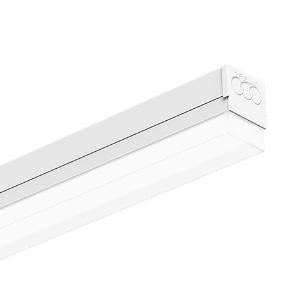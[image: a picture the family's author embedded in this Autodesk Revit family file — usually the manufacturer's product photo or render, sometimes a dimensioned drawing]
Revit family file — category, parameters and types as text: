
# Revit family: 3f_filippi_-_3f_zeta_dr_3f_filippi_-_10986_-_3f_zeta_dr_2x22_led_ep_l1489
name_source: partatom
category: Lighting Fixtures
units: mm (PartAtom-declared; Revit-internal decimal feet)

## family parameters
Cut with Voids When Loaded = No
Host = Face
Light Source = No
Part Type = Normal
Room Calculation Point = No
Round Connector Dimension = Use Diameter
Shared = No

## types (1)
- 3F Filippi - 3F Zeta DR (1 x LED, 6253 lm, 50 W, 4000 K)
    Apparent Load = 50 VA
    Approval mark = ENEC
    CIE Flux Codes = 41 72 91 86 100
    Color Rendering = 80
    Color Temperature = 4000 K
    Control Gear = Electronic ballast
    Default Elevation = 1800 mm
    Description = ILLUMINOTECHNICAL
Luminous efficiency 100% (DLOR 86%, ULOR 14%).
Initial luminous flux of the luminaire 6253 lm.
Emergency luminaire luminous flux BLF 7.6%.
Diffused symmetric distribution.
Installation Interdistance Transv.D = 1.31 x hu - Long.D = 1.25 x hu.
Tabular UGR (CIE 117 - 4H-8H; S=0.25H; 70/50/20): RUG 25.7 - 24.2.
Beam angle: 136° - 112°.
Luminous efficacy 125 lm/W.
Lifetime (L93/B10): 30000 h. (tq+25°C)
Lifetime (L90/B10): 50000 h. (tq+25°C)
Lifetime (L85/B10): 80000 h. (tq+25°C)
Lifetime (L80/B10): 100000 h. (tq+25°C)
Sudden decreased luminous flux after 50000 hours: 0% (C0).
Photobiological safety in compliance with IEC/TR 62778: RG0 risk exempt, (IEC 62471).
In compliance with IEC/EN 62722-2-1 - IEC/EN 62717 standards.

SOURCE
2 linear LED modules 22W/840.
Energy efficiency class (UE 2019/2020 - UE 2019/2015): D.
CIE 13.3 Colour rendering index: CRI >80 (R9 <50%).
IES TM-30 Fidelity Index: Rf = 84 Rg = 95.
CCT nominal colour temperature 4000 K.
Colour initial tolerance (MacAdam): SDCM 3.

MECHANICAL
Housing in hot-galvanised steel, painted in white polyester, obtained through rolling process.
Light unit in hot-galvanised steel, painted in white polyester base with fixing springs and retractable safety hooks in stainless steel.
Rectangular screen in self-extinguishing polycarbonate, UV stabilised, opal, with smooth outer surface.
End caps in white polycarbonate.
Pair of stainless steel sliding brackets with sliding block screws.
Luminaire with limited surface temperature. - D - (EN 60598-2-24)
Dimensions: 1489x62 mm, height 81 mm. Weight 4.76 kg.
IP40 protection degree.
Mechanical strength to impacts IK06 (1 joule).
Glow-wire test resistance 850°C.

ELECTRICAL
Halogen Free electronic wiring 230V-50/60Hz, power factor 0.90, THD <25%, constant output current, SELV, class I, 1 driver.
Power of the luminaire 50 W.
CE - IEC 60598-1 - EN 60598-1.
EP maintained emergency wiring on board, 1h duration, 24h recharge; compliant with EN 60598-2-22, excluding high risk areas.
SAFE FLICKER: PstLM=<1 and SVM=<0.4 (IEC TR 61547-1 and IEC TR 63158), to ensure a more comfortable and safe light.
Ambient temperature from +5°C to +25°C.
Temperature class T6 max 85°C.
Relative humidity UR: <85%.

INSTALLATION
Ceiling / Suspended / Wall.
All accessories dedicated to this product are available on the Catalog and on our website www.3F-Filippi.com.

APPLICATIONS
Suitable product for food production plants (HACCP), IFS (Food Version 6), BRC (GSFS Food Version 7).
In commercial environments, exhibition areas, shops and stores.

WARNING
Luminaire designed for disposal/recycling at end-of-life.
Replaceable (LED only) light source by a professional. Replaceable control gear by a professional.
    Height = 81 mm
    Lamp = 1 x LED
    Lamp Light Flux = 6253 lm
    Lamp Power = 50 W
    Lamp count = 1
    Length = 1489 mm
    Lifetime = 50000 h
    Luminous efficacy = 125 lm/W
    Manufacturer = 3F Filippi
    ModVariant = No
    Model = 3F Filippi - 10986 - 3F Zeta DR 2x22 LED EP L1489
    Mounting Place = Ceiling
    Mounting Type = Pendant
    Number of Poles = 1
    OnlyDefault = Yes
    Power Factor = 1
    Product Name = 3F Filippi - 3F Zeta DR
    Product group = pendant luminaire
    ProductGroupID = 9
    Protection Class = Protection class I
    Protection Degree = IP 40
    RLX_Detail_Level = 1
    RLX_Emergency_Light_Flux = 0 lm
    RLX_Emergency_Type = 0
    RLX_Emergency_Type_DB = No
    RlxData = <blob elided: 32741 chars, md5=ae899501>
    Socket = socket
    Standby Power = 0 W
    System Light Flux = 6253 lm
    System Power = 50 W
    Type Comments = Product without accessories
    Type Image = 3ffilippi_3f_zeta_dr.jpg
    URL = http://relux.com
    VarID = ---
    Voltage = 0 V
    Weight = 0.00 kg
    Width = 62 mm  [stored 0.203412 ft]

note: [stored X ft] marks values corroborated as IEEE doubles in the binary element streams (Revit-internal decimal feet)

## geometry (parser evidence)
native form markers: Blend x4, Sweep x12
no freeform markers — native parametric forms only
